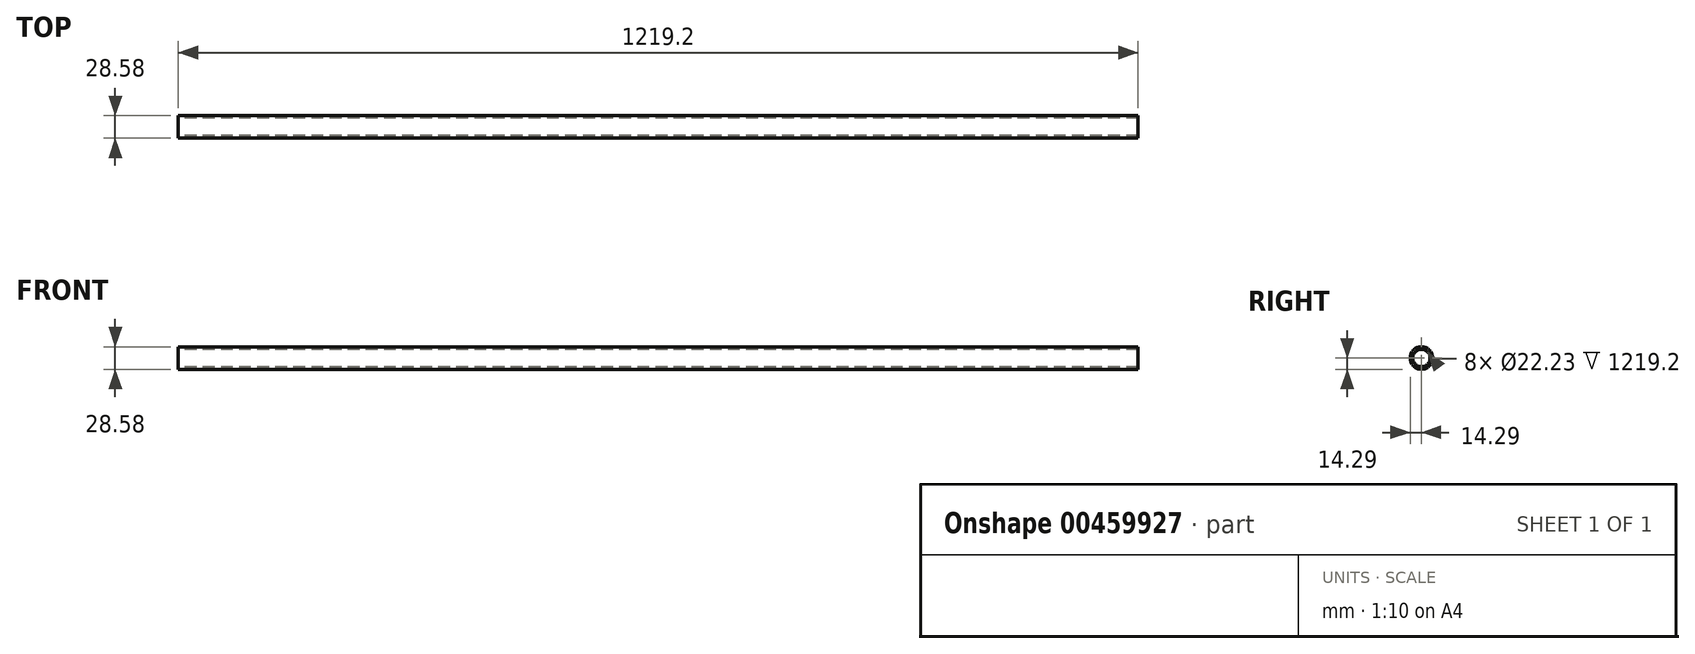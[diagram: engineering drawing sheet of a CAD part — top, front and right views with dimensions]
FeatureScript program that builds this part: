
annotation { "Feature Type Name" : "Feature", "Feature Type Description" : "" }
export const myFeature = defineFeature(function(context is Context, id is Id, definition is map)
    precondition{}
    {
        {
            var Q0;
            Q0=qCreatedBy(makeId("Right.planeOp"),FACE);
            var sketch = newSketch(context, id + "F0", { "sketchPlane" : qUnion([Q0])});
            skCircle(sketch, "E0", {"center": v(0, 0) * mm, "radius": 14.29 * mm});
            skCircle(sketch, "E1", {"center": v(0, 0) * mm, "radius": 11.11 * mm});
            skSolve(sketch);
        }
        {
            var Q0;
            Q0=makeQuery(id+"F0.imprint","IMPRINT",FACE,{"disambiguationData":[TD([[makeQuery(id+"F0.imprint","IMPRINT",EDGE,{"derivedFrom":sQuery(id+"F0.wireOp",EDGE,"E0")}),1.0]])]});
            extrude(context, id + "F1", {"entities" : qUnion([Q0]), "endBound" : BoundingType.SYMMETRIC, "depth" : 1219.2 * mm});
        }
    });
